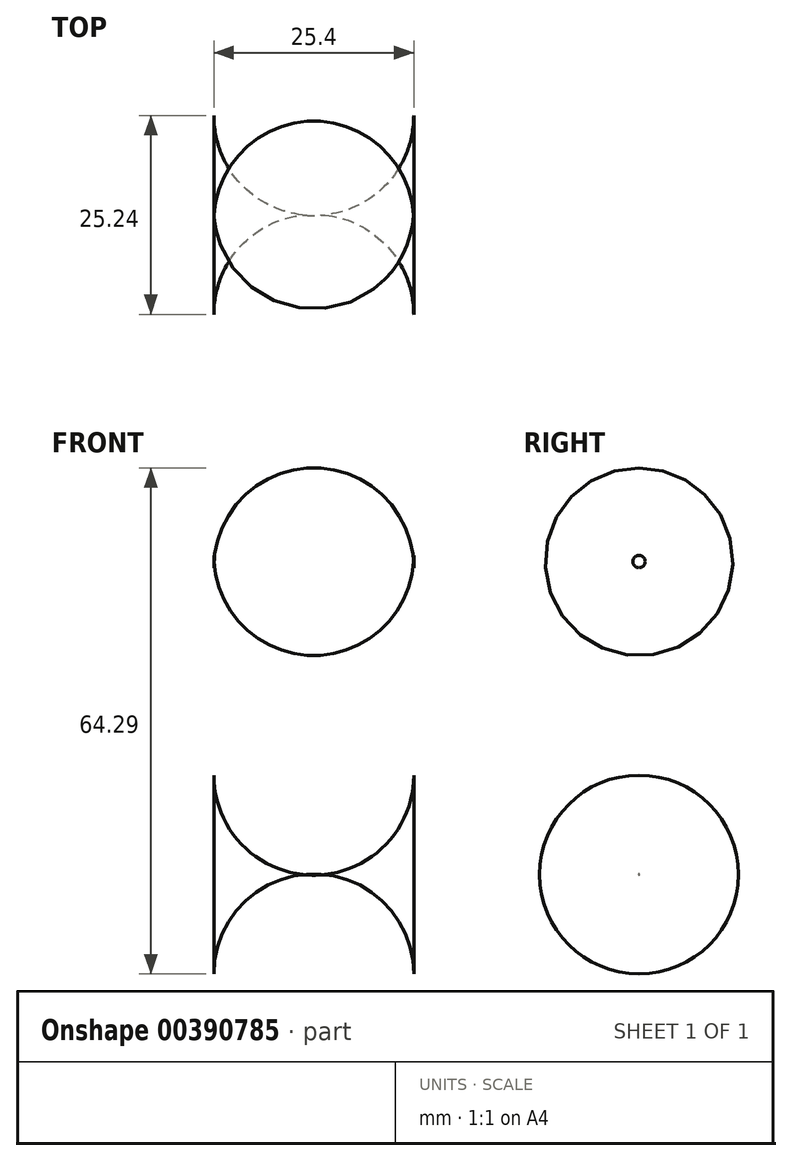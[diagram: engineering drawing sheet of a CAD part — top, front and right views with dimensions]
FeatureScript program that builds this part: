
annotation { "Feature Type Name" : "Feature", "Feature Type Description" : "" }
export const myFeature = defineFeature(function(context is Context, id is Id, definition is map)
    precondition{}
    {
        {
            var Q0;
            Q0=qCreatedBy(makeId("Right.planeOp"),FACE);
            var sketch = newSketch(context, id + "F0", { "sketchPlane" : qUnion([Q0])});
            skCircle(sketch, "E0", {"center": v(0, 0) * mm, "radius": 25.32 * mm});
            skSolve(sketch);
        }
        {
            var Q0;
            Q0=makeQuery(id+"F0.imprint","IMPRINT",FACE,{"disambiguationData":[TD([[makeQuery(id+"F0.imprint","IMPRINT",EDGE,{"derivedFrom":sQuery(id+"F0.wireOp",EDGE,"E0")}),1.0]])]});
            extrude(context, id + "F1", {"entities" : qUnion([Q0]), "depth" : 25.4 * mm});
        }
        {
            var Q0;
            Q0=makeQuery(id+"F1.opExtrude","SWEPT_FACE",FACE,{"disambiguationData":[OSD([sQuery(id+"F0.wireOp",EDGE,"E0")])]});
            fillet(context, id + "F2", {"entities" : qUnion([Q0]), "radius" : 12.7 * mm, "tangentPropagation" : true, "allowEdgeOverflow" : false});
        }
        {
            var Q0;
            Q0=qCreatedBy(makeId("Right.planeOp"),FACE);
            var sketch = newSketch(context, id + "F3", { "sketchPlane" : qUnion([Q0])});
            skCircle(sketch, "E1", {"center": v(0, 39.75) * mm, "radius": 13.48 * mm});
            skSolve(sketch);
        }
        {
            var Q0;
            Q0=makeQuery(id+"F3.imprint","IMPRINT",FACE,{"disambiguationData":[TD([[makeQuery(id+"F3.imprint","IMPRINT",EDGE,{"derivedFrom":sQuery(id+"F3.wireOp",EDGE,"E1")}),1.0]])]});
            extrude(context, id + "F4", {"entities" : qUnion([Q0]), "depth" : 25.4 * mm});
        }
        {
            var Q0;
            Q0=makeQuery(id+"F4.opExtrude","SWEPT_FACE",FACE,{"disambiguationData":[OSD([sQuery(id+"F3.wireOp",EDGE,"E1")])]});
            fillet(context, id + "F5", {"entities" : qUnion([Q0]), "radius" : 12.7 * mm, "tangentPropagation" : true, "allowEdgeOverflow" : false});
        }
    });
